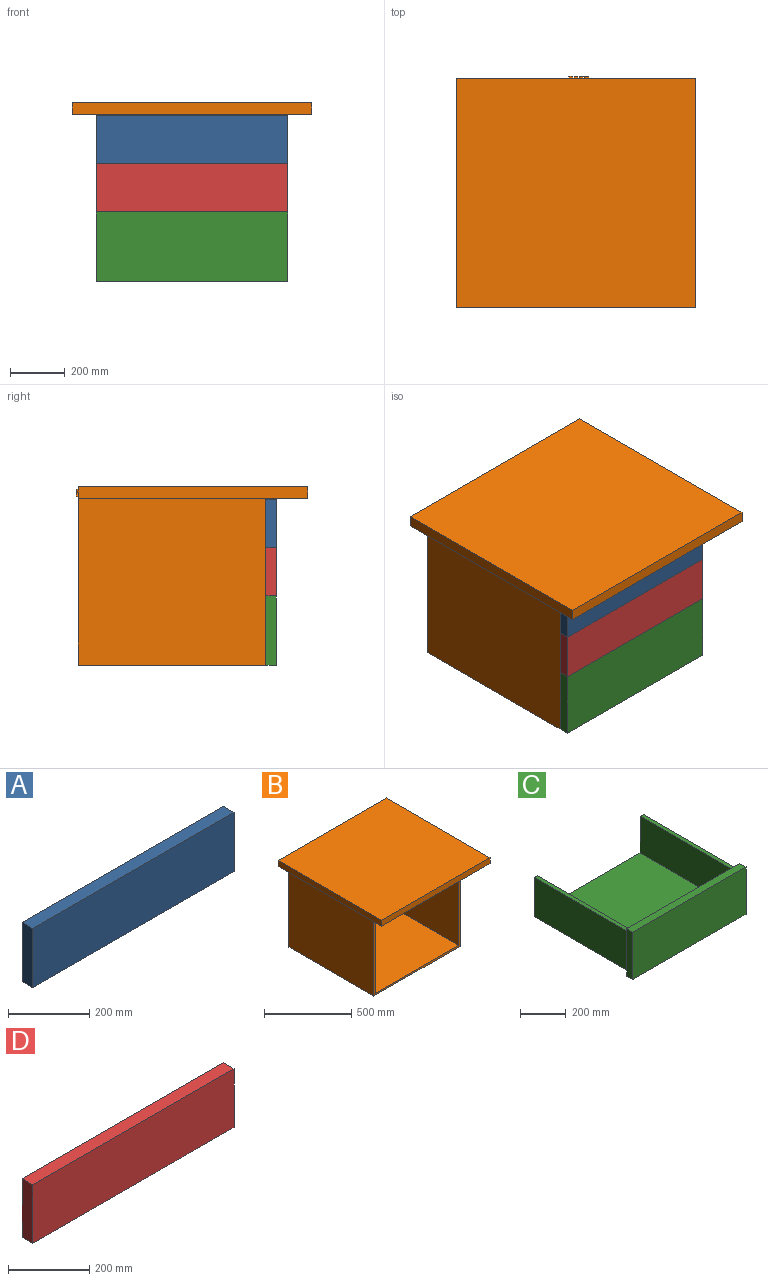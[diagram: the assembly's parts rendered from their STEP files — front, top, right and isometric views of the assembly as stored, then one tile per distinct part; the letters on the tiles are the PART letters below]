
ASSEMBLY  parts=4 mates=9
PART A: 6 faces, bbox 698.5x38.1x177.8 mm
  f0: plane 177.8x38.1mm, normal (-1,0,0), area 6774.2mm2, adj f1,f3,f4,f5
  f1: plane 698.5x38.1mm, normal (0,0,-1), area 26612.8mm2, adj f0,f2,f4,f5
  f2: plane 177.8x38.1mm, normal (1,0,0), area 6774.2mm2, adj f1,f3,f4,f5
  f3: plane 698.5x38.1mm, normal (0,0,1), area 26612.8mm2, adj f0,f2,f4,f5
  f4: plane 698.5x177.8mm, normal (0,-1,0), area 124193.3mm2, adj f0,f1,f2,f3
  f5: plane 698.5x177.8mm, normal (0,1,0), area 124193.3mm2, adj f0,f1,f2,f3
PART B: 103 faces, bbox 876.3x844.6x650.9 mm
  f0: plane 673.1x596.9mm, normal (-1,0,0), area 401773.4mm2, adj f1,f8,f98,f102
  f1: plane 673.1x596.9mm, normal (0,-1,0), area 401773.4mm2, adj f0,f2,f8,f102
  f2: plane 673.1x596.9mm, normal (1,0,0), area 401773.4mm2, adj f1,f8,f98,f102
  f3: plane 876.3x650.88mm, normal (0,1,0), area 461148.1mm2, adj f4,f5,f7,f8,f21,f22,f23,f24
  f4: plane 838.2x41.28mm, normal (1,0,0), area 34596.7mm2, adj f3,f6,f7,f8
  f5: plane 838.2x41.28mm, normal (-1,0,0), area 34596.7mm2, adj f3,f6,f7,f8
  f6: plane 876.3x41.28mm, normal (0,-1,0), area 36169.3mm2, adj f4,f5,f7,f8
  f7: plane 876.3x838.2mm, normal (0,0,1), area 734514.7mm2, adj f3,f4,f5,f6
  f8: plane 876.3x838.2mm, normal (0,0,-1), area 708547mm2, adj f0,f1,f2,f3,f4,f5,f6,f98
  f9: plane 9.43x6.35mm, normal (-1,0,0), area 59.9mm2, adj f10,f33,f34,f36
  f10: plane 6.35x5.02mm, normal (0,0,-1), area 31.9mm2, adj f9,f11,f34,f36
  f11: extruded ~6.35x4.8mm, area 31.7mm2, adj f10,f12,f34,f36
  f12: extruded ~6.35x3.45mm, area 25.1mm2, adj f11,f13,f34,f36
  f13: extruded ~6.35x3.7mm, area 26.4mm2, adj f12,f14,f34,f36
  f14: extruded ~6.35x4.59mm, area 30.6mm2, adj f13,f33,f34,f36
  f15: plane 6.35x4.82mm, normal (0,0,1), area 30.6mm2, adj f16,f31,f34,f35
  f16: plane 8.25x6.35mm, normal (-1,0,0), area 52.4mm2, adj f15,f17,f34,f35
  f17: plane 6.35x4.31mm, normal (0,0,-1), area 27.4mm2, adj f16,f18,f34,f35
  f18: extruded ~6.35x4.82mm, area 31.6mm2, adj f17,f19,f34,f35
  f19: extruded ~6.35x3.06mm, area 22.7mm2, adj f18,f20,f34,f35
  f20: extruded ~6.35x3.28mm, area 23.5mm2, adj f19,f31,f34,f35
  f21: plane 7.12x6.35mm, normal (0,0,1), area 45.2mm2, adj f3,f22,f32,f34
  f22: plane 25.19x6.35mm, normal (1,0,0), area 159.9mm2, adj f3,f21,f23,f34
  f23: plane 8.79x6.35mm, normal (0,0,-1), area 55.8mm2, adj f3,f22,f24,f34
  f24: extruded ~6.38x6.35mm, area 43.2mm2, adj f3,f23,f25,f34
  f25: extruded ~6.35x5.27mm, area 37.8mm2, adj f3,f24,f26,f34
  f26: extruded ~6.35x6.03mm, area 58.5mm2, adj f3,f25,f27,f34
  f27: plane 6.35x0.17mm, normal (-1,0,0), area 1.1mm2, adj f3,f26,f28,f34
  f28: extruded ~6.35x3.65mm, area 26.6mm2, adj f3,f27,f29,f34
  f29: extruded ~6.35x3.7mm, area 25.3mm2, adj f3,f28,f30,f34
  f30: extruded ~6.35x4.74mm, area 34.8mm2, adj f3,f29,f32,f34
  f31: extruded ~6.35x4.47mm, area 29.4mm2, adj f15,f20,f34,f35
  f32: extruded ~7.25x6.35mm, area 47.6mm2, adj f3,f21,f30,f34
  f33: plane 6.35x5.26mm, normal (0,0,1), area 33.4mm2, adj f9,f14,f34,f36
  f34: plane 25.19x17.45mm, normal (0,1,0), area 216.3mm2, adj f9,f10,f11,f12,f13,f14,f15,f16
  f35: plane 10.65x8.25mm, normal (0,1,0), area 80.2mm2, adj f15,f16,f17,f18,f19,f20,f31
  f36: plane 11.39x9.43mm, normal (0,1,0), area 97.8mm2, adj f9,f10,f11,f12,f13,f14,f33
  f37: extruded ~6.35x4.2mm, area 29mm2, adj f38,f63,f64,f65
  f38: extruded ~6.35x2.62mm, area 17.8mm2, adj f37,f39,f64,f65
  f39: extruded ~6.35x2.36mm, area 16.7mm2, adj f38,f40,f64,f65
  f40: extruded ~6.35x2.92mm, area 21.9mm2, adj f39,f41,f64,f65
  f41: extruded ~6.35x4.92mm, area 32.3mm2, adj f40,f42,f64,f65
  f42: plane 6.35x2.86mm, normal (-0.04,0,-1), area 18.2mm2, adj f41,f43,f64,f65
  f43: plane 6.35x1.7mm, normal (1,0,0), area 10.8mm2, adj f42,f63,f64,f65
  f44: plane 6.35x2.69mm, normal (0.98,0,-0.21), area 17.5mm2, adj f3,f45,f62,f64
  f45: plane 6.35x2.12mm, normal (0,0,-1), area 13.5mm2, adj f3,f44,f46,f64
  f46: plane 12.89x6.35mm, normal (-1,0,0), area 81.8mm2, adj f3,f45,f47,f64
  f47: extruded ~6.35x4.8mm, area 33.2mm2, adj f3,f46,f48,f64
  f48: extruded ~6.35x5mm, area 33.9mm2, adj f3,f47,f49,f64
  f49: extruded ~6.35x3.34mm, area 21.4mm2, adj f3,f48,f50,f64
  f50: extruded ~6.35x3.06mm, area 20.9mm2, adj f3,f49,f51,f64
  f51: plane 6.35x2.19mm, normal (0.93,0,-0.37), area 15mm2, adj f3,f50,f52,f64
  f52: extruded ~6.35x5.34mm, area 35.4mm2, adj f3,f51,f53,f64
  f53: extruded ~6.35x3.06mm, area 21.2mm2, adj f3,f52,f54,f64
  f54: extruded ~6.35x3.28mm, area 22.2mm2, adj f3,f53,f55,f64
  f55: plane 6.35x1.17mm, normal (1,0,0), area 7.5mm2, adj f3,f54,f56,f64
  f56: plane 6.35x3.2mm, normal (0.03,0,1), area 20.3mm2, adj f3,f55,f57,f64
  f57: extruded ~9.14x6.35mm, area 78mm2, adj f3,f56,f58,f64
  f58: extruded ~6.35x4.12mm, area 28.9mm2, adj f3,f57,f59,f64
  f59: extruded ~6.35x4.4mm, area 30.1mm2, adj f3,f58,f60,f64
  f60: extruded ~6.35x3.51mm, area 22.8mm2, adj f3,f59,f61,f64
  f61: extruded ~6.35x2.81mm, area 23.7mm2, adj f3,f60,f62,f64
  f62: plane 6.35x0.14mm, normal (0,0,-1), area 0.9mm2, adj f3,f44,f61,f64
  f63: extruded ~6.35x4.1mm, area 28.6mm2, adj f37,f43,f64,f65
  f64: plane 19.54x15.14mm, normal (0,1,0), area 139.6mm2, adj f37,f38,f39,f40,f41,f42,f43,f44
  f65: plane 9.28x7.27mm, normal (0,1,0), area 54.4mm2, adj f37,f38,f39,f40,f41,f42,f43,f63
  f66: extruded ~6.35x6.35mm, area 44.8mm2, adj f3,f67,f80,f81
  f67: extruded ~6.35x4.77mm, area 31.2mm2, adj f3,f66,f68,f81
  f68: plane 6.35x2.53mm, normal (-1,0,0), area 16.1mm2, adj f3,f67,f69,f81
  f69: extruded ~6.35x4.84mm, area 31.6mm2, adj f3,f68,f70,f81
  f70: extruded ~6.35x4.16mm, area 30.1mm2, adj f3,f69,f71,f81
  f71: extruded ~6.35x5.34mm, area 35.7mm2, adj f3,f70,f72,f81
  f72: extruded ~7.34x6.35mm, area 67.7mm2, adj f3,f71,f73,f81
  f73: extruded ~6.35x1.98mm, area 12.7mm2, adj f3,f72,f74,f81
  f74: extruded ~6.35x2.07mm, area 13.7mm2, adj f3,f73,f75,f81
  f75: plane 6.35x2.43mm, normal (-0.94,0,-0.34), area 16.4mm2, adj f3,f74,f76,f81
  f76: extruded ~6.35x2.13mm, area 14.3mm2, adj f3,f75,f77,f81
  f77: extruded ~6.35x2.72mm, area 17.4mm2, adj f3,f76,f78,f81
  f78: extruded ~6.5x6.35mm, area 45.9mm2, adj f3,f77,f79,f81
  f79: extruded ~7.32x6.35mm, area 49.8mm2, adj f3,f78,f80,f81
  f80: extruded ~7.14x6.35mm, area 48.6mm2, adj f3,f66,f79,f81
  f81: plane 19.57x13.64mm, normal (0,1,0), area 94.5mm2, adj f66,f67,f68,f69,f70,f71,f72,f73
  f82: extruded ~6.35x2.76mm, area 22.6mm2, adj f3,f83,f96,f97
  f83: plane 6.35x0.14mm, normal (0,0,1), area 0.9mm2, adj f3,f82,f84,f97
  f84: extruded ~6.35x2.93mm, area 18.6mm2, adj f3,f83,f85,f97
  f85: plane 14.22x6.35mm, normal (-1,0,0), area 90.3mm2, adj f3,f84,f86,f97
  f86: plane 6.35x2.83mm, normal (0,0,1), area 18mm2, adj f3,f85,f87,f97
  f87: plane 26.81x6.35mm, normal (1,0,0), area 170.2mm2, adj f3,f86,f88,f97
  f88: plane 6.35x2.83mm, normal (0,0,-1), area 18mm2, adj f3,f87,f89,f97
  f89: plane 7.06x6.35mm, normal (-1,0,0), area 44.8mm2, adj f3,f88,f90,f97
  f90: plane 6.35x2.15mm, normal (-0.65,0,-0.76), area 18.1mm2, adj f3,f89,f91,f97
  f91: plane 8.92x6.67mm, normal (0.8,0,-0.6), area 70.7mm2, adj f3,f90,f92,f97
  f92: plane 6.35x3.46mm, normal (0,0,-1), area 22mm2, adj f3,f91,f93,f97
  f93: plane 10.84x8.19mm, normal (-0.8,0,0.6), area 86.2mm2, adj f3,f92,f94,f97
  f94: plane 8.04x7.65mm, normal (-0.72,0,-0.69), area 70.5mm2, adj f3,f93,f95,f97
  f95: plane 6.35x3.4mm, normal (0,0,1), area 21.6mm2, adj f3,f94,f96,f97
  f96: plane 6.46x6.35mm, normal (0.73,0,0.69), area 56.4mm2, adj f3,f82,f95,f97
  f97: plane 26.81x15.11mm, normal (0,1,0), area 143.9mm2, adj f82,f83,f84,f85,f86,f87,f88,f89
  f98: plane 698.5x609.6mm, normal (0,-1,0), area 24032.2mm2, adj f0,f2,f8,f99,f100,f101,f102
  f99: plane 685.8x609.6mm, normal (-1,0,0), area 418063.7mm2, adj f3,f8,f98,f101
  f100: plane 685.8x609.6mm, normal (1,0,0), area 418063.7mm2, adj f3,f8,f98,f101
  f101: plane 698.5x685.8mm, normal (0,0,-1), area 479031.3mm2, adj f3,f98,f99,f100
  f102: plane 673.1x673.1mm, normal (0,0,1), area 453063.6mm2, adj f0,f1,f2,f98
PART C: 15 faces, bbox 698.5x622.3x252.4 mm
  f0: plane 252.41x38.1mm, normal (-1,0,0), area 9616.9mm2, adj f1,f3,f4,f5
  f1: plane 698.5x38.1mm, normal (0,0,-1), area 26612.8mm2, adj f0,f2,f4,f5
  f2: plane 252.41x38.1mm, normal (1,0,0), area 9616.9mm2, adj f1,f3,f4,f5
  f3: plane 698.5x38.1mm, normal (0,0,1), area 26612.8mm2, adj f0,f2,f4,f5
  f4: plane 698.5x252.41mm, normal (0,-1,0), area 176310.1mm2, adj f0,f1,f2,f3
  f5: plane 698.5x252.41mm, normal (0,1,0), area 160261.8mm2, adj f0,f1,f2,f3,f6,f7,f8,f9
  f6: plane 584.2x209.55mm, normal (1,0,0), area 122419.1mm2, adj f5,f7,f13,f14
  f7: plane 673.1x584.2mm, normal (0,0,-1), area 393225mm2, adj f5,f6,f8,f14
  f8: plane 584.2x209.55mm, normal (-1,0,0), area 122419.1mm2, adj f5,f7,f9,f14
  f9: plane 584.2x19.05mm, normal (0,0,1), area 11129mm2, adj f5,f8,f10,f14
  f10: plane 584.2x196.85mm, normal (1,0,0), area 114999.8mm2, adj f5,f9,f11,f14
  f11: plane 635x584.2mm, normal (0,0,1), area 370967mm2, adj f5,f10,f12,f14
  f12: plane 584.2x196.85mm, normal (-1,0,0), area 114999.8mm2, adj f5,f11,f13,f14
  f13: plane 584.2x19.05mm, normal (0,0,1), area 11129mm2, adj f5,f6,f12,f14
  f14: plane 673.1x209.55mm, normal (0,1,0), area 16048.4mm2, adj f6,f7,f8,f9,f10,f11,f12,f13
PART D: 6 faces, bbox 698.5x38.1x176.2 mm
  f0: plane 176.21x38.1mm, normal (-1,0,0), area 6713.7mm2, adj f1,f3,f4,f5
  f1: plane 698.5x38.1mm, normal (0,0,-1), area 26612.8mm2, adj f0,f2,f4,f5
  f2: plane 176.21x38.1mm, normal (1,0,0), area 6713.7mm2, adj f1,f3,f4,f5
  f3: plane 698.5x38.1mm, normal (0,0,1), area 26612.8mm2, adj f0,f2,f4,f5
  f4: plane 698.5x176.21mm, normal (0,-1,0), area 123084.4mm2, adj f0,f1,f2,f3
  f5: plane 698.5x176.21mm, normal (0,1,0), area 123084.4mm2, adj f0,f1,f2,f3
PLACE A t=(0,-685.8,-3.17)mm
PLACE B t=(0,-419.1,609.6)mm
PLACE C t=(0,-685.8,0)mm
PLACE D t=(0,-685.8,-1.59)mm
MATE planar C.f1 <-> B.f101  axis (0,0,-1) through (0,-704.85,0)mm
MATE planar A.f1 <-> D.f3  axis (0,0,-1) through (0,-704.85,428.62)mm
MATE slider C.f5 <-> B.f98  axis (0,1,0) through (0,-685.8,0)mm
MATE planar D.f2 <-> B.f100  axis (1,0,0) through (349.25,-704.85,340.52)mm
MATE planar D.f1 <-> C.f3  axis (0,0,-1) through (0,-704.85,252.41)mm
MATE planar A.f4 <-> D.f4  axis (0,-1,0) through (0,-723.9,517.52)mm
MATE planar C.f2 <-> B.f100  axis (1,0,0) through (349.25,-704.85,126.21)mm
MATE planar A.f2 <-> D.f2  axis (1,0,0) through (349.25,-704.85,517.52)mm
MATE planar D.f4 <-> C.f4  axis (0,-1,0) through (0,-723.9,340.52)mm
